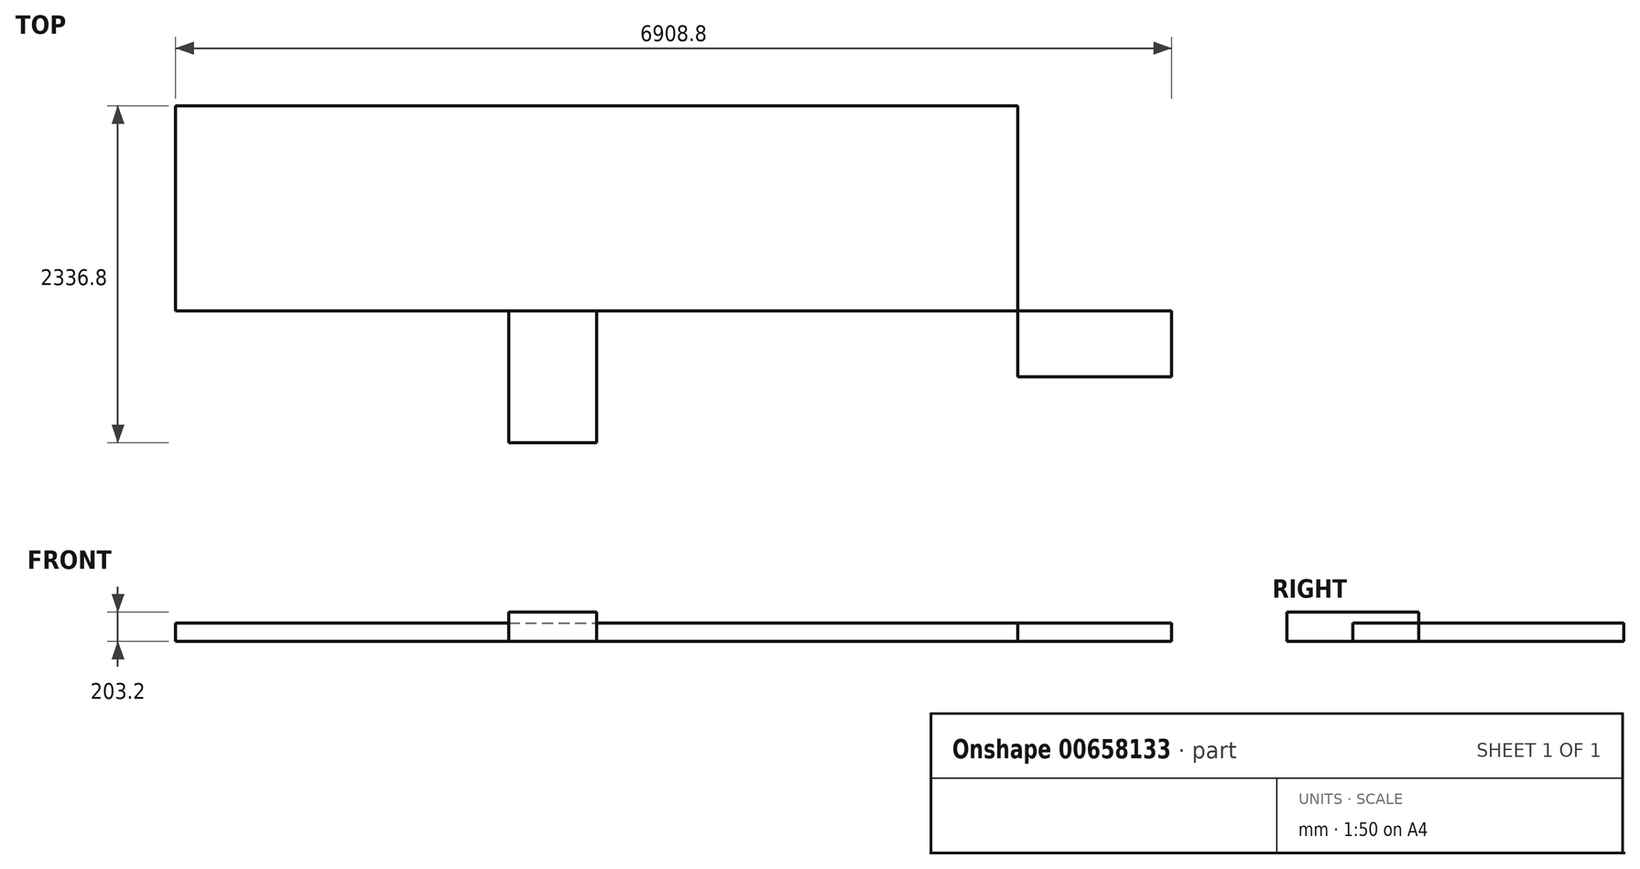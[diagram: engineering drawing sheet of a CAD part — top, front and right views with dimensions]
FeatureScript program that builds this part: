
annotation { "Feature Type Name" : "Feature", "Feature Type Description" : "" }
export const myFeature = defineFeature(function(context is Context, id is Id, definition is map)
    precondition{}
    {
        {
            var Q0;
            Q0=qCreatedBy(makeId("Top.planeOp"),FACE);
            var sketch = newSketch(context, id + "F0", { "sketchPlane" : qUnion([Q0])});
            skLineSegment(sketch, "E0.bottom", {"start": v(0, 0) * mm, "end": v(5842, 0) * mm});
            skLineSegment(sketch, "E0.top", {"start": v(0, 1422.4) * mm, "end": v(5842, 1422.4) * mm});
            skLineSegment(sketch, "E0.left", {"start": v(0, 0) * mm, "end": v(0, 1422.4) * mm});
            skLineSegment(sketch, "E0.right", {"start": v(5842, 0) * mm, "end": v(5842, 1422.4) * mm});
            skSolve(sketch);
        }
        {
            var Q0;
            Q0 = qSketchRegion(id + "F0", true);
            extrude(context, id + "F1", {"entities" : qUnion([Q0]), "depth" : 127 * mm, "offsetDistance" : 25.4 * mm});
        }
        {
            var Q0;
            Q0=makeQuery(id+"F1.opExtrude","CAP_FACE",FACE,{"disambiguationData":[OSD([sQuery(id+"F0.wireOp",EDGE,"E0.bottom"),sQuery(id+"F0.wireOp",EDGE,"E0.top"),sQuery(id+"F0.wireOp",EDGE,"E0.left"),sQuery(id+"F0.wireOp",EDGE,"E0.right")])],"isStart":false});
            var sketch = newSketch(context, id + "F2", { "sketchPlane" : qUnion([Q0])});
            skPoint(sketch, "E1", {"position": v(2311.4, 0) * mm});
            skPoint(sketch, "E2.oppositeSnap0", {"position": v(2921, 0) * mm});
            skLineSegment(sketch, "E2.bottom", {"start": v(2311.4, 0) * mm, "end": v(2921, 0) * mm});
            skLineSegment(sketch, "E2.top", {"start": v(2311.4, -914.4) * mm, "end": v(2921, -914.4) * mm});
            skLineSegment(sketch, "E2.left", {"start": v(2311.4, 0) * mm, "end": v(2311.4, -914.4) * mm});
            skLineSegment(sketch, "E2.right", {"start": v(2921, 0) * mm, "end": v(2921, -914.4) * mm});
            skSolve(sketch);
        }
        {
            var Q0;
            Q0 = qSketchRegion(id + "F2", true);
            extrude(context, id + "F3", {"entities" : qUnion([Q0]), "oppositeDirection" : true, "depth" : 127 * mm, "offsetDistance" : 25.4 * mm, "hasSecondDirection" : true, "secondDirectionOppositeDirection" : false, "secondDirectionDepth" : 76.2 * mm});
        }
        {
            var Q0;
            Q0=makeQuery(id+"F1.opExtrude","CAP_FACE",FACE,{"disambiguationData":[OSD([sQuery(id+"F0.wireOp",EDGE,"E0.bottom"),sQuery(id+"F0.wireOp",EDGE,"E0.top"),sQuery(id+"F0.wireOp",EDGE,"E0.left"),sQuery(id+"F0.wireOp",EDGE,"E0.right")])],"isStart":false});
            var sketch = newSketch(context, id + "F4", { "sketchPlane" : qUnion([Q0])});
            skLineSegment(sketch, "E3.bottom", {"start": v(5842, 0) * mm, "end": v(6908.8, 0) * mm});
            skLineSegment(sketch, "E3.top", {"start": v(5842, -457.2) * mm, "end": v(6908.8, -457.2) * mm});
            skLineSegment(sketch, "E3.left", {"start": v(5842, 0) * mm, "end": v(5842, -457.2) * mm});
            skLineSegment(sketch, "E3.right", {"start": v(6908.8, 0) * mm, "end": v(6908.8, -457.2) * mm});
            skSolve(sketch);
        }
        {
            var Q0;
            Q0 = qSketchRegion(id + "F4", true);
            extrude(context, id + "F5", {"entities" : qUnion([Q0]), "oppositeDirection" : true, "depth" : 127 * mm, "offsetDistance" : 25.4 * mm});
        }
    });
